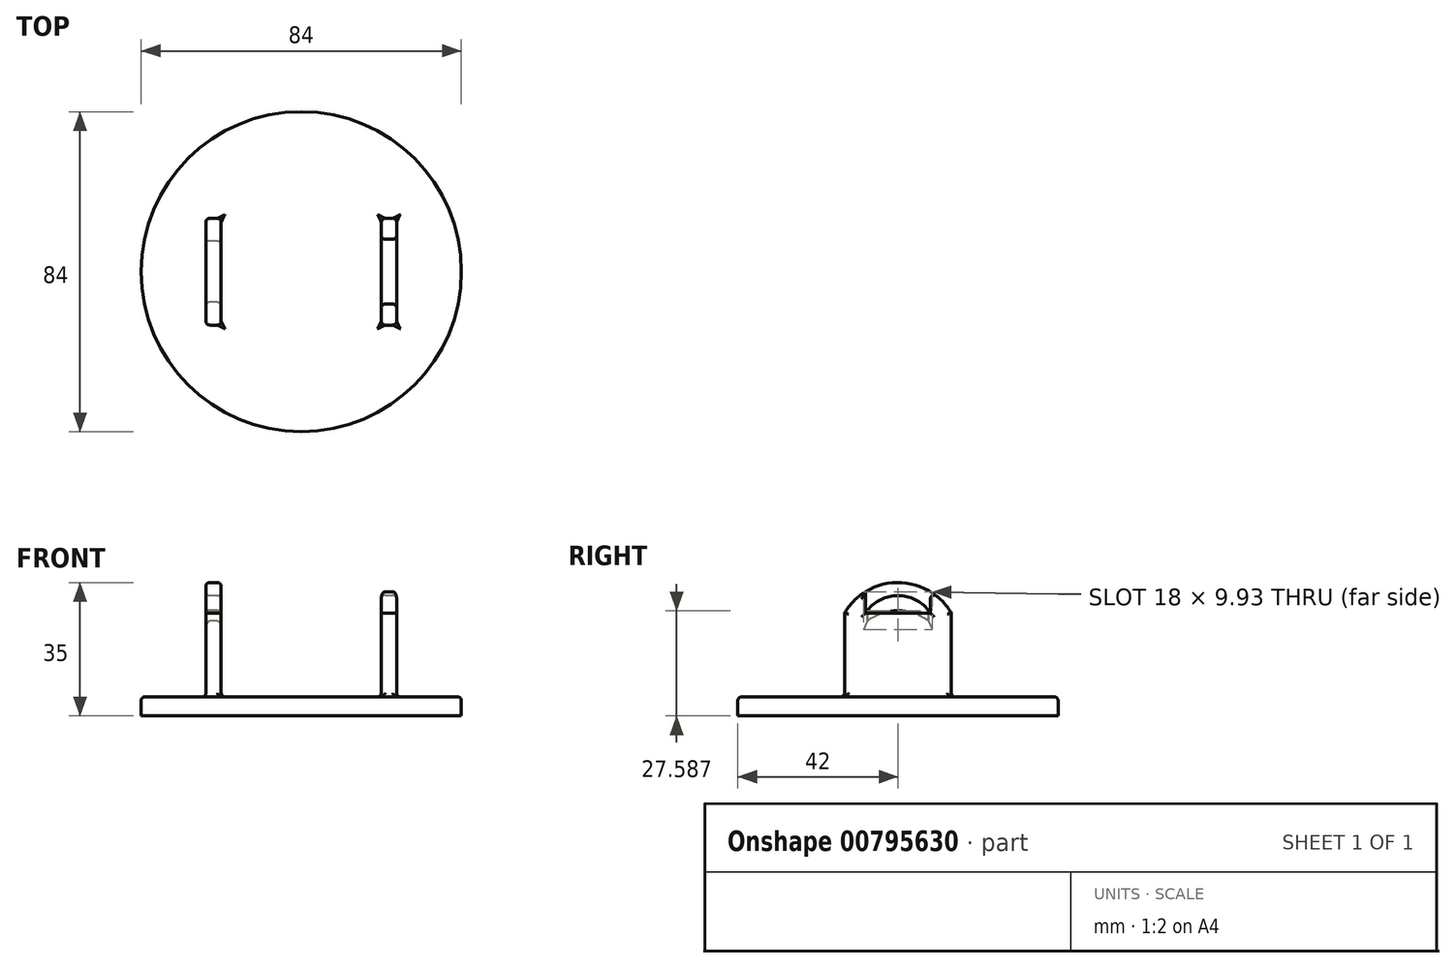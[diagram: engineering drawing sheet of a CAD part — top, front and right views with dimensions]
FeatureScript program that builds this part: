
annotation { "Feature Type Name" : "Feature", "Feature Type Description" : "" }
export const myFeature = defineFeature(function(context is Context, id is Id, definition is map)
    precondition{}
    {
        {
            var Q0;
            Q0=qCreatedBy(makeId("Top.planeOp"),FACE);
            var sketch = newSketch(context, id + "F0", { "sketchPlane" : qUnion([Q0])});
            skCircle(sketch, "E0", {"center": v(0, 0) * mm, "radius": 42 * mm});
            skSolve(sketch);
        }
        {
            var Q0;
            Q0=makeQuery(id+"F0.imprint","IMPRINT",FACE,{"disambiguationData":[TD([[makeQuery(id+"F0.imprint","IMPRINT",EDGE,{"derivedFrom":sQuery(id+"F0.wireOp",EDGE,"E0")}),1.0]])]});
            extrude(context, id + "F1", {"entities" : qUnion([Q0]), "depth" : 5 * mm, "offsetDistance" : 25 * mm});
        }
        {
            var Q0;
            Q0=makeQuery(id+"F1.opExtrude","CAP_FACE",FACE,{"disambiguationData":[OSD([sQuery(id+"F0.wireOp",EDGE,"E0")])],"isStart":false});
            var sketch = newSketch(context, id + "F2", { "sketchPlane" : qUnion([Q0])});
            skLineSegment(sketch, "E1.bottom", {"start": v(-25, 14) * mm, "end": v(-21, 14) * mm});
            skLineSegment(sketch, "E1.top", {"start": v(-25, -14) * mm, "end": v(-21, -14) * mm});
            skLineSegment(sketch, "E1.left", {"start": v(-25, 14) * mm, "end": v(-25, -14) * mm});
            skLineSegment(sketch, "E1.right", {"start": v(-21, 14) * mm, "end": v(-21, -14) * mm});
            skLineSegment(sketch, "E2.bottom", {"start": v(21, 14) * mm, "end": v(25, 14) * mm});
            skLineSegment(sketch, "E2.top", {"start": v(21, -14) * mm, "end": v(25, -14) * mm});
            skLineSegment(sketch, "E2.left", {"start": v(21, 14) * mm, "end": v(21, -14) * mm});
            skLineSegment(sketch, "E2.right", {"start": v(25, 14) * mm, "end": v(25, -14) * mm});
            skSolve(sketch);
        }
        {
            var Q0;
            Q0=makeQuery(id+"F2.imprint","IMPRINT",FACE,{"disambiguationData":[TD([[makeQuery(id+"F2.imprint","IMPRINT",EDGE,{"derivedFrom":sQuery(id+"F2.wireOp",EDGE,"E1.bottom")}),-1.0]])]});
            var Q1;
            Q1=makeQuery(id+"F2.imprint","IMPRINT",FACE,{"disambiguationData":[TD([[makeQuery(id+"F2.imprint","IMPRINT",EDGE,{"derivedFrom":sQuery(id+"F2.wireOp",EDGE,"E2.bottom")}),-1.0]])]});
            extrude(context, id + "F3", {"entities" : qUnion([Q0, Q1]), "operationType" : NewBodyOperationType.ADD, "depth" : 30 * mm, "offsetDistance" : 25 * mm});
        }
        {
            var Q0;
            Q0=makeQuery(id+"F3.opExtrude","SWEPT_FACE",FACE,{"disambiguationData":[OSD([sQuery(id+"F2.wireOp",EDGE,"E2.right")])]});
            var sketch = newSketch(context, id + "F4", { "sketchPlane" : qUnion([Q0])});
            skArc(sketch, "E3", {"start": v(14, 27) * mm, "mid": v(0, 35) * mm, "end": v(-14, 27) * mm});
            skSolve(sketch);
        }
        {
            var Q0;
            {var subQ0=sQuery(id+"F4.wireOp",EDGE,"E3");var subQ1=sQuery(id+"F2.wireOp",EDGE,"E2.right");var subQ4=makeQuery(id+"F3.opExtrude","CAP_EDGE",EDGE,{"disambiguationData":[OSD([subQ1])],"isStart":false});var subQ5=makeQuery(id+"F4.imprint","INTERSECT",VERTEX,{"derivedFrom":[subQ4,subQ0]});Q0=makeQuery(id+"F4.imprint","IMPRINT",FACE,{"disambiguationData":[TD([[makeQuery(id+"F4.imprint","IMPRINT",EDGE,{"disambiguationData":[TD([[subQ5,-1.0]])],"derivedFrom":subQ0}),-1.0]])]});}
            var Q1;
            {var subQ0=sQuery(id+"F4.wireOp",EDGE,"E3");var subQ1=sQuery(id+"F2.wireOp",EDGE,"E2.right");var subQ4=makeQuery(id+"F3.opExtrude","CAP_EDGE",EDGE,{"disambiguationData":[OSD([subQ1])],"isStart":false});var subQ5=makeQuery(id+"F4.imprint","INTERSECT",VERTEX,{"derivedFrom":[subQ4,subQ0]});Q1=makeQuery(id+"F4.imprint","IMPRINT",FACE,{"disambiguationData":[TD([[makeQuery(id+"F4.imprint","IMPRINT",EDGE,{"disambiguationData":[TD([[subQ5,1.0]])],"derivedFrom":subQ0}),-1.0]])]});}
            extrude(context, id + "F5", {"entities" : qUnion([Q0, Q1]), "operationType" : NewBodyOperationType.REMOVE, "oppositeDirection" : true, "depth" : 59.4 * mm, "offsetDistance" : 25 * mm});
        }
        {
            var Q0;
            Q0=makeQuery(id+"F3.opExtrude","SWEPT_FACE",FACE,{"disambiguationData":[OSD([sQuery(id+"F2.wireOp",EDGE,"E1.left")])]});
            var sketch = newSketch(context, id + "F6", { "sketchPlane" : qUnion([Q0])});
            skArc(sketch, "E4", {"start": v(8, 27.68) * mm, "mid": v(0, 31.55) * mm, "end": v(-8, 27.68) * mm});
            skLineSegment(sketch, "E5", {"start": v(8, 27.68) * mm, "end": v(8, 24.88) * mm});
            skLineSegment(sketch, "E6", {"start": v(-8, 27.68) * mm, "end": v(-8, 24.88) * mm});
            skPoint(sketch, "E7.center.orphan", {"position": v(0, 25.17) * mm});
            skArc(sketch, "E8", {"start": v(8, 24.88) * mm, "mid": v(0, 27.57) * mm, "end": v(-8, 24.88) * mm});
            skSolve(sketch);
        }
        {
            var Q0;
            Q0 = qSketchRegion(id + "F6", true);
            extrude(context, id + "F7", {"entities" : qUnion([Q0]), "operationType" : NewBodyOperationType.REMOVE, "oppositeDirection" : true, "depth" : 5.8 * mm, "offsetDistance" : 25 * mm});
        }
        {
            var Q0;
            Q0=makeQuery(id+"F3.opExtrude","SWEPT_FACE",FACE,{"disambiguationData":[OSD([sQuery(id+"F2.wireOp",EDGE,"E2.right")])]});
            var sketch = newSketch(context, id + "F8", { "sketchPlane" : qUnion([Q0])});
            skLineSegment(sketch, "E9.bottom", {"start": v(-8.5, 36) * mm, "end": v(8.5, 36) * mm});
            skLineSegment(sketch, "E9.top", {"start": v(-8.5, 27) * mm, "end": v(8.5, 27) * mm});
            skLineSegment(sketch, "E9.left", {"start": v(-8.5, 36) * mm, "end": v(-8.5, 27) * mm});
            skLineSegment(sketch, "E9.right", {"start": v(8.5, 36) * mm, "end": v(8.5, 27) * mm});
            skSolve(sketch);
        }
        {
            var Q0;
            {var subQ0=sQuery(id+"F8.wireOp",EDGE,"E9.top");Q0=makeQuery(id+"F8.imprint","IMPRINT",FACE,{"disambiguationData":[TD([[makeQuery(id+"F8.imprint","IMPRINT",EDGE,{"derivedFrom":subQ0}),1.0]])]});}
            extrude(context, id + "F9", {"entities" : qUnion([Q0]), "operationType" : NewBodyOperationType.REMOVE, "oppositeDirection" : true, "depth" : 6 * mm, "offsetDistance" : 25 * mm});
        }
        {
            var Q0;
            Q0=makeQuery(id+"F7.boolean.opBoolean","INTERSECT",EDGE,{"derivedFrom":[makeQuery(id+"F3.opExtrude","SWEPT_FACE",FACE,{"disambiguationData":[OSD([sQuery(id+"F2.wireOp",EDGE,"E1.right")])]}),makeQuery(id+"F7.opExtrude","SWEPT_FACE",FACE,{"disambiguationData":[OSD([sQuery(id+"F6.wireOp",EDGE,"E4")])]})]});
            var Q1;
            Q1=makeQuery(id+"F7.boolean.opBoolean","INTERSECT",EDGE,{"derivedFrom":[makeQuery(id+"F3.opExtrude","SWEPT_FACE",FACE,{"disambiguationData":[OSD([sQuery(id+"F2.wireOp",EDGE,"E1.right")])]}),makeQuery(id+"F7.opExtrude","SWEPT_FACE",FACE,{"disambiguationData":[OSD([sQuery(id+"F6.wireOp",EDGE,"E7")])]})]});
            var Q2;
            Q2=makeQuery(id+"F7.boolean.opBoolean","INTERSECT",EDGE,{"derivedFrom":[makeQuery(id+"F3.opExtrude","SWEPT_FACE",FACE,{"disambiguationData":[OSD([sQuery(id+"F2.wireOp",EDGE,"E1.right")])]}),makeQuery(id+"F7.opExtrude","SWEPT_FACE",FACE,{"disambiguationData":[OSD([sQuery(id+"F6.wireOp",EDGE,"E6")])]})]});
            var Q3;
            Q3=makeQuery(id+"F7.boolean.opBoolean","INTERSECT",EDGE,{"derivedFrom":[makeQuery(id+"F3.opExtrude","SWEPT_FACE",FACE,{"disambiguationData":[OSD([sQuery(id+"F2.wireOp",EDGE,"E1.right")])]}),makeQuery(id+"F7.opExtrude","SWEPT_FACE",FACE,{"disambiguationData":[OSD([sQuery(id+"F6.wireOp",EDGE,"E5")])]})]});
            var Q4;
            Q4=makeQuery(id+"F3.opExtrude","SWEPT_FACE",FACE,{"disambiguationData":[OSD([sQuery(id+"F2.wireOp",EDGE,"E1.left")])]});
            var Q5;
            Q5=makeQuery(id+"F3.opExtrude","CAP_EDGE",EDGE,{"disambiguationData":[OSD([sQuery(id+"F2.wireOp",EDGE,"E1.right")])],"isStart":true});
            var Q6;
            Q6=makeQuery(id+"F1.opExtrude","CAP_FACE",FACE,{"disambiguationData":[OSD([sQuery(id+"F0.wireOp",EDGE,"E0")])],"isStart":false});
            fillet(context, id + "F10", {"entities" : qUnion([Q0, Q1, Q2, Q3, Q4, Q5, Q6]), "radius" : 1 * mm, "tangentPropagation" : true, "allowEdgeOverflow" : false});
        }
        {
            var Q0;
            Q0=makeQuery(id+"F9.boolean.opBoolean","COPY",EDGE,{"derivedFrom":makeQuery(id+"F9.opExtrude","SWEPT_EDGE",EDGE,{"disambiguationData":[OSD([sQuery(id+"F4.wireOp",EDGE,"E3"),sQuery(id+"F8.wireOp",EDGE,"E9.right")])]})});
            var Q1;
            Q1=makeQuery(id+"F9.boolean.opBoolean","COPY",EDGE,{"derivedFrom":makeQuery(id+"F9.opExtrude","SWEPT_EDGE",EDGE,{"disambiguationData":[OSD([sQuery(id+"F4.wireOp",EDGE,"E3"),sQuery(id+"F8.wireOp",EDGE,"E9.left")])]})});
            var Q2;
            Q2=makeQuery(id+"F9.boolean.opBoolean","COPY",EDGE,{"derivedFrom":makeQuery(id+"F9.opExtrude","CAP_EDGE",EDGE,{"disambiguationData":[OSD([sQuery(id+"F8.wireOp",EDGE,"E9.top")])],"isStart":true})});
            var Q3;
            Q3=makeQuery(id+"F9.boolean.opBoolean","INTERSECT",EDGE,{"derivedFrom":[makeQuery(id+"F3.opExtrude","SWEPT_FACE",FACE,{"disambiguationData":[OSD([sQuery(id+"F2.wireOp",EDGE,"E2.left")])]}),makeQuery(id+"F9.opExtrude","SWEPT_FACE",FACE,{"disambiguationData":[OSD([sQuery(id+"F8.wireOp",EDGE,"E9.top")])]})]});
            var Q4;
            Q4=makeQuery(id+"F9.boolean.opBoolean","COPY",EDGE,{"derivedFrom":makeQuery(id+"F9.opExtrude","CAP_EDGE",EDGE,{"disambiguationData":[OSD([sQuery(id+"F8.wireOp",EDGE,"E9.right")])],"isStart":true})});
            var Q5;
            Q5=makeQuery(id+"F9.boolean.opBoolean","INTERSECT",EDGE,{"derivedFrom":[makeQuery(id+"F3.opExtrude","SWEPT_FACE",FACE,{"disambiguationData":[OSD([sQuery(id+"F2.wireOp",EDGE,"E2.left")])]}),makeQuery(id+"F9.opExtrude","SWEPT_FACE",FACE,{"disambiguationData":[OSD([sQuery(id+"F8.wireOp",EDGE,"E9.right")])]})]});
            var Q6;
            Q6=makeQuery(id+"F9.boolean.opBoolean","INTERSECT",EDGE,{"derivedFrom":[makeQuery(id+"F3.opExtrude","SWEPT_FACE",FACE,{"disambiguationData":[OSD([sQuery(id+"F2.wireOp",EDGE,"E2.left")])]}),makeQuery(id+"F9.opExtrude","SWEPT_FACE",FACE,{"disambiguationData":[OSD([sQuery(id+"F8.wireOp",EDGE,"E9.left")])]})]});
            var Q7;
            Q7=makeQuery(id+"F9.boolean.opBoolean","COPY",EDGE,{"derivedFrom":makeQuery(id+"F9.opExtrude","CAP_EDGE",EDGE,{"disambiguationData":[OSD([sQuery(id+"F8.wireOp",EDGE,"E9.left")])],"isStart":true})});
            var Q8;
            Q8=makeQuery(id+"F3.opExtrude","SWEPT_FACE",FACE,{"disambiguationData":[OSD([sQuery(id+"F2.wireOp",EDGE,"E2.right")])]});
            var Q9;
            Q9=makeQuery(id+"F3.opExtrude","SWEPT_FACE",FACE,{"disambiguationData":[OSD([sQuery(id+"F2.wireOp",EDGE,"E2.left")])]});
            var Q10;
            Q10=makeQuery(id+"F3.opExtrude","SWEPT_FACE",FACE,{"disambiguationData":[OSD([sQuery(id+"F2.wireOp",EDGE,"E1.right")])]});
            fillet(context, id + "F11", {"entities" : qUnion([Q0, Q1, Q2, Q3, Q4, Q5, Q6, Q7, Q8, Q9, Q10]), "radius" : 1 * mm, "tangentPropagation" : true, "allowEdgeOverflow" : false});
        }
    });
